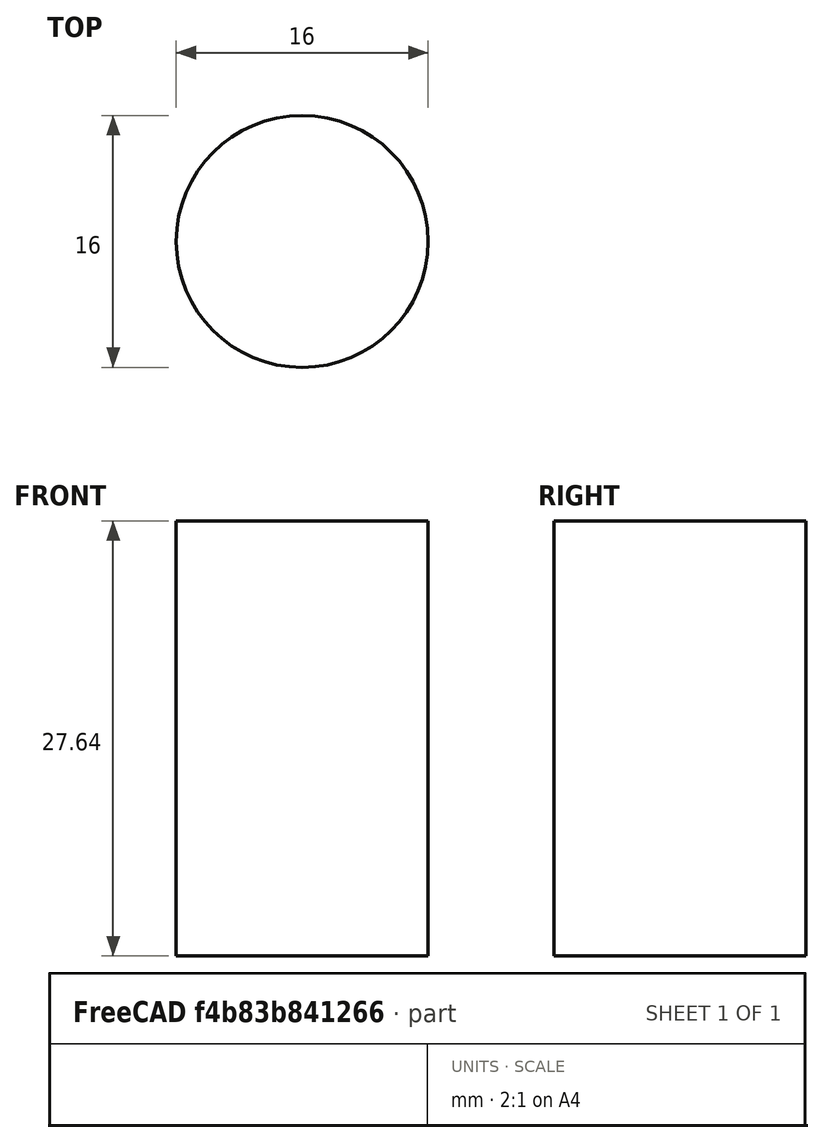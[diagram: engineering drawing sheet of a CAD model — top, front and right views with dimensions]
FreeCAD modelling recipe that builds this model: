
FCSTD DOCUMENT  (FreeCAD 0.19R24267 +99 (Git))
Label: M16x1_5 static compression plate stud
License: All rights reserved
LicenseURL: http://en.wikipedia.org/wiki/All_rights_reserved
objects: PartDesign::Pad×2, Sketcher::SketchObject×1, PartDesign::Body×1
note: 6 computed .brp shape members not serialized (recipe doc carries the construction recipe); baked Part::Feature solids carry a one-line shape summary decoded from their .brp

FEATURE [Sketcher::SketchObject] Sketch
  FullyConstrained = true
  MapMode = 5
  Support = -> [XY_Plane]
  sketch-geometry (1):
    g0: Circle CenterX=0 CenterY=0 CenterZ=0 NormalX=0 NormalY=0 NormalZ=1 AngleXU=0 Radius=8
  constraints (2):
    c: Coincident(g0,g-1)
    c: Diameter(g0) = 16
FEATURE [PartDesign::Pad] Pad  label="Compression plate engagement"
  Direction = (1,1,1)
  Length = 15.64
  Length2 = 100
  Profile = -> Sketch
  Type = 0
FEATURE [PartDesign::Pad] Pad001  label=" Load cell or coupling section"
  BaseFeature = -> Pad
  Direction = (1,1,1)
  Length = 12
  Length2 = 100
  Profile = -> Pad [Face3]
  Type = 0
FEATURE [PartDesign::Body] Body
  Group = -> [Sketch,Pad,Pad001]
  Origin = -> Origin
  Tip = -> Pad001
